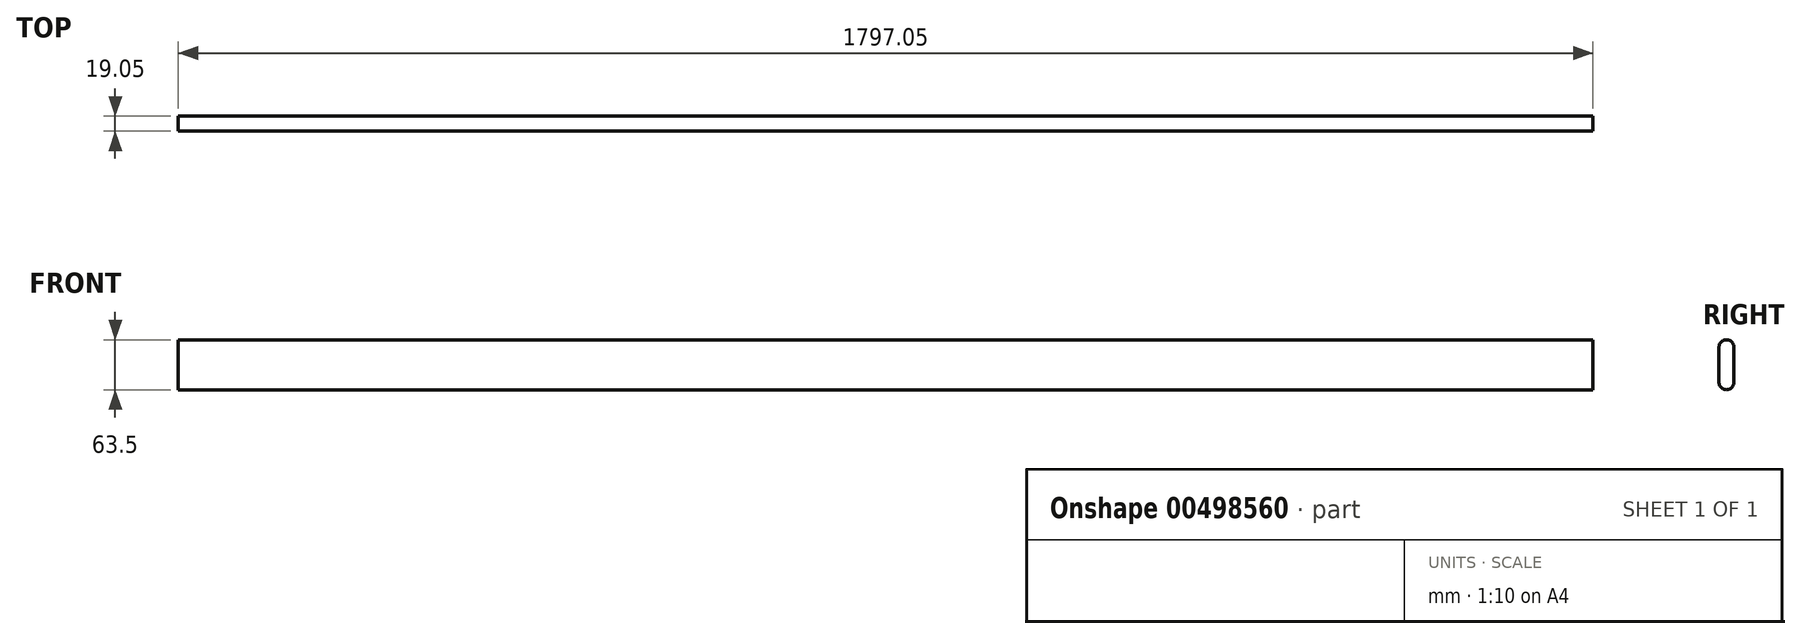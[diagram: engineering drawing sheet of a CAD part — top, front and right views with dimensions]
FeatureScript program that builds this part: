
annotation { "Feature Type Name" : "Feature", "Feature Type Description" : "" }
export const myFeature = defineFeature(function(context is Context, id is Id, definition is map)
    precondition{}
    {
        {
            var Q0;
            Q0=qCreatedBy(makeId("Front.planeOp"),FACE);
            var sketch = newSketch(context, id + "F0", { "sketchPlane" : qUnion([Q0])});
            skLineSegment(sketch, "E0.bottom", {"start": v(0, 0) * mm, "end": v(1797.05, 0) * mm});
            skLineSegment(sketch, "E0.top", {"start": v(0, 63.5) * mm, "end": v(1797.05, 63.5) * mm});
            skLineSegment(sketch, "E0.left", {"start": v(0, 0) * mm, "end": v(0, 63.5) * mm});
            skLineSegment(sketch, "E0.right", {"start": v(1797.05, 0) * mm, "end": v(1797.05, 63.5) * mm});
            skSolve(sketch);
        }
        {
            var Q0;
            Q0 = qSketchRegion(id + "F0", true);
            extrude(context, id + "F1", {"entities" : qUnion([Q0]), "depth" : 19.05 * mm, "offsetDistance" : 25.4 * mm});
        }
        {
            var Q0;
            Q0=makeQuery(id+"F1.opExtrude","CAP_EDGE",EDGE,{"disambiguationData":[OSD([sQuery(id+"F0.wireOp",EDGE,"E0.top")])],"isStart":false});
            var Q1;
            Q1=makeQuery(id+"F1.opExtrude","CAP_EDGE",EDGE,{"disambiguationData":[OSD([sQuery(id+"F0.wireOp",EDGE,"E0.top")])],"isStart":true});
            var Q2;
            Q2=makeQuery(id+"F1.opExtrude","CAP_EDGE",EDGE,{"disambiguationData":[OSD([sQuery(id+"F0.wireOp",EDGE,"E0.bottom")])],"isStart":false});
            var Q3;
            Q3=makeQuery(id+"F1.opExtrude","CAP_EDGE",EDGE,{"disambiguationData":[OSD([sQuery(id+"F0.wireOp",EDGE,"E0.bottom")])],"isStart":true});
            fillet(context, id + "F2", {"entities" : qUnion([Q0, Q1, Q2, Q3]), "radius" : 9.52 * mm, "tangentPropagation" : true, "allowEdgeOverflow" : false});
        }
    });
